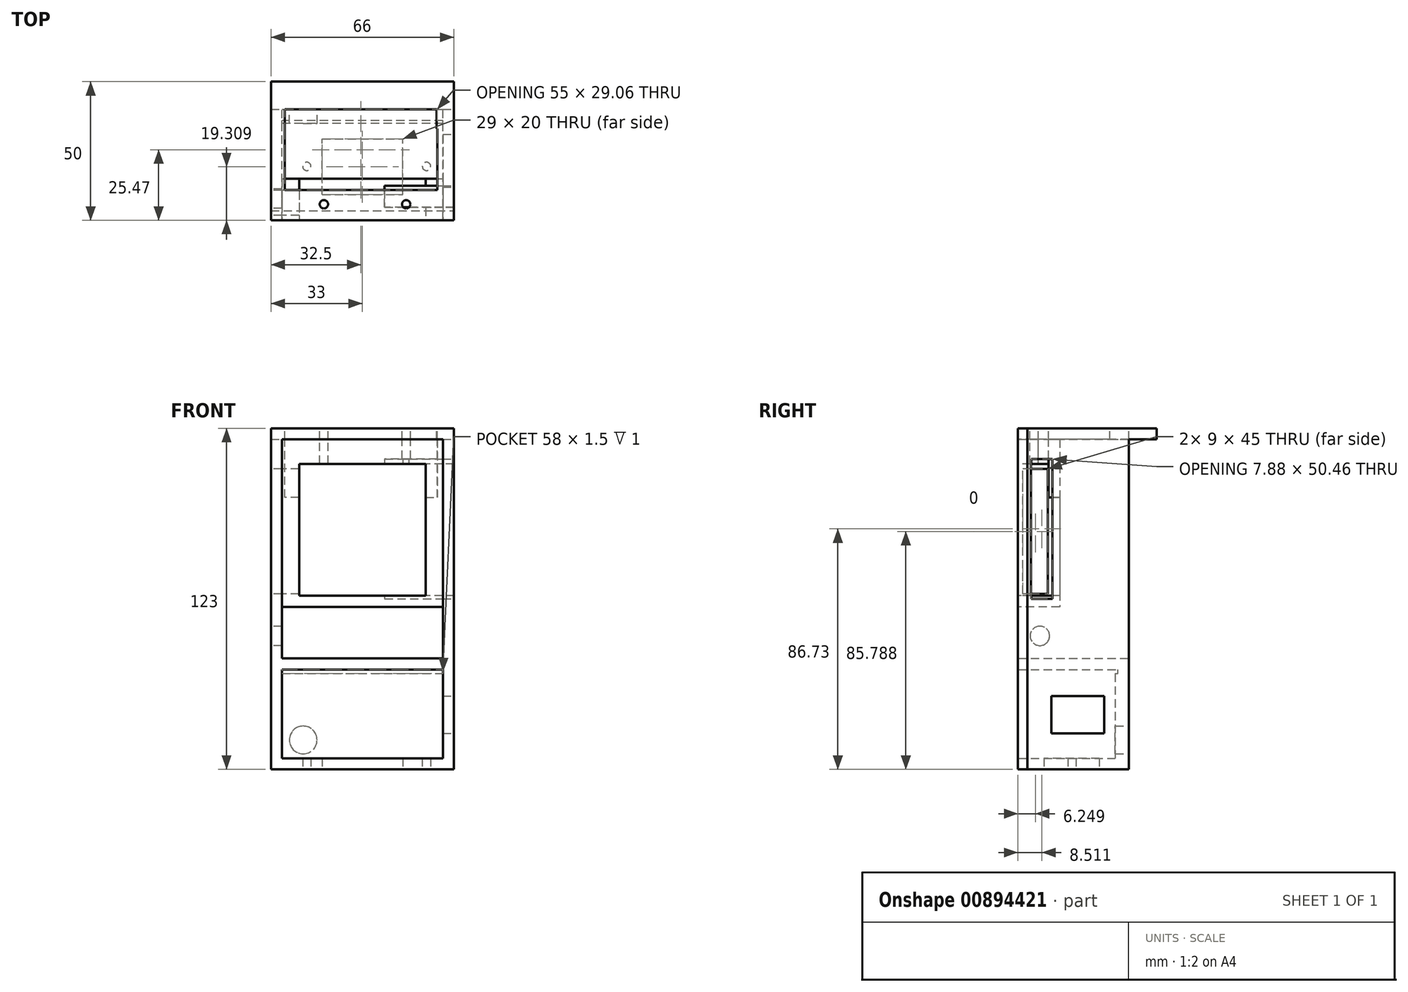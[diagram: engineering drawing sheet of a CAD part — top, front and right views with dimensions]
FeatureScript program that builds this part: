
annotation { "Feature Type Name" : "Feature", "Feature Type Description" : "" }
export const myFeature = defineFeature(function(context is Context, id is Id, definition is map)
    precondition{}
    {
        {
            var Q0;
            Q0=qCreatedBy(makeId("Front.planeOp"),FACE);
            var sketch = newSketch(context, id + "F0", { "sketchPlane" : qUnion([Q0])});
            skLineSegment(sketch, "E0.bottom", {"start": v(-29, 57.5) * mm, "end": v(29, 57.5) * mm});
            skLineSegment(sketch, "E0.top", {"start": v(-29, -57.5) * mm, "end": v(29, -57.5) * mm});
            skLineSegment(sketch, "E0.left", {"start": v(-29, 57.5) * mm, "end": v(-29, -57.5) * mm});
            skLineSegment(sketch, "E0.right", {"start": v(29, 57.5) * mm, "end": v(29, -57.5) * mm});
            skPoint(sketch, "E0.middle", {"position": v(0, 0) * mm});
            skLineSegment(sketch, "E1.0", {"start": v(-33, 61.5) * mm, "end": v(33, 61.5) * mm});
            skLineSegment(sketch, "E1.1", {"start": v(-33, 61.5) * mm, "end": v(-33, -61.5) * mm});
            skLineSegment(sketch, "E1.2", {"start": v(-33, -61.5) * mm, "end": v(33, -61.5) * mm});
            skLineSegment(sketch, "E1.3", {"start": v(33, 61.5) * mm, "end": v(33, -61.5) * mm});
            skLineSegment(sketch, "E2.bottom", {"start": v(-29, -21.5) * mm, "end": v(29, -21.5) * mm});
            skLineSegment(sketch, "E2.top", {"start": v(-29, -25.5) * mm, "end": v(29, -25.5) * mm});
            skLineSegment(sketch, "E2.left", {"start": v(-29, -21.5) * mm, "end": v(-29, -25.5) * mm});
            skLineSegment(sketch, "E2.right", {"start": v(29, -21.5) * mm, "end": v(29, -25.5) * mm});
            skPoint(sketch, "E3.end.orphan", {"position": v(-11.95, -21.5) * mm});
            skLineSegment(sketch, "E4", {"start": v(21.26, 35.1) * mm, "end": v(20.76, 35.1) * mm});
            skLineSegment(sketch, "E5.bottom", {"start": v(-21, 46.17) * mm, "end": v(21.26, 46.17) * mm});
            skLineSegment(sketch, "E5.top", {"start": v(-21, -2.9) * mm, "end": v(21.26, -2.9) * mm});
            skLineSegment(sketch, "E5.left", {"start": v(-21, 46.17) * mm, "end": v(-21, -2.9) * mm});
            skLineSegment(sketch, "E5.right", {"start": v(21.26, 46.17) * mm, "end": v(21.26, -2.9) * mm});
            skLineSegment(sketch, "E6", {"start": v(-29, -2.9) * mm, "end": v(-21, -2.9) * mm});
            skLineSegment(sketch, "E7", {"start": v(21.26, -2.9) * mm, "end": v(29, -2.9) * mm});
            skPoint(sketch, "E8.end.orphan", {"position": v(11.45, 46.17) * mm});
            skPoint(sketch, "E9.end.orphan", {"position": v(-21, 32.08) * mm});
            skLineSegment(sketch, "E10", {"start": v(0, 57.5) * mm, "end": v(0, -21.5) * mm});
            skSolve(sketch);
        }
        {
            var Q0;
            {var subQ6=sQuery(id+"F0.wireOp",EDGE,"E0.bottom");Q0=makeQuery(id+"F0.imprint","IMPRINT",FACE,{"disambiguationData":[TD([[makeQuery(id+"F0.imprint","IMPRINT",EDGE,{"derivedFrom":subQ6}),1.0]])]});}
            var Q1;
            Q1=makeQuery(id+"F0.imprint","IMPRINT",FACE,{"disambiguationData":[TD([[makeQuery(id+"F0.imprint","IMPRINT",EDGE,{"derivedFrom":sQuery(id+"F0.wireOp",EDGE,"E2.bottom")}),-1.0]])]});
            extrude(context, id + "F1", {"entities" : qUnion([Q0, Q1]), "depth" : 40 * mm, "offsetDistance" : 25 * mm});
        }
        {
            var Q0;
            Q0=makeQuery(id+"F1.opExtrude","CAP_FACE",FACE,{"disambiguationData":[OSD([sQuery(id+"F0.wireOp",EDGE,"E0.bottom"),sQuery(id+"F0.wireOp",EDGE,"E0.top"),sQuery(id+"F0.wireOp",EDGE,"E0.left"),sQuery(id+"F0.wireOp",EDGE,"E0.right"),sQuery(id+"F0.wireOp",EDGE,"E1.0"),sQuery(id+"F0.wireOp",EDGE,"E1.1"),sQuery(id+"F0.wireOp",EDGE,"E1.2"),sQuery(id+"F0.wireOp",EDGE,"E1.3"),sQuery(id+"F0.wireOp",EDGE,"E2.bottom"),sQuery(id+"F0.wireOp",EDGE,"E2.top")])],"isStart":false});
            var sketch = newSketch(context, id + "F2", { "sketchPlane" : qUnion([Q0])});
            skLineSegment(sketch, "E11", {"start": v(7.17, -21.5) * mm, "end": v(7.17, -1.5) * mm});
            skLineSegment(sketch, "E12.bottom", {"start": v(-22.77, 48.68) * mm, "end": v(22.77, 48.68) * mm});
            skLineSegment(sketch, "E12.top", {"start": v(-22.77, -2.9) * mm, "end": v(22.77, -2.9) * mm});
            skLineSegment(sketch, "E12.left", {"start": v(-22.77, 48.68) * mm, "end": v(-22.77, -2.9) * mm});
            skLineSegment(sketch, "E12.right", {"start": v(22.77, 48.68) * mm, "end": v(22.77, -2.9) * mm});
            skPoint(sketch, "E13.end.orphan", {"position": v(-17.23, 48.68) * mm});
            skPoint(sketch, "E14.end.orphan", {"position": v(-22.77, 26.8) * mm});
            skLineSegment(sketch, "E15.bottom", {"start": v(-29, -2.9) * mm, "end": v(29, -2.9) * mm});
            skLineSegment(sketch, "E15.top", {"start": v(-29, 1.1) * mm, "end": v(29, 1.1) * mm});
            skLineSegment(sketch, "E15.left", {"start": v(-29, -2.9) * mm, "end": v(-29, 1.1) * mm});
            skLineSegment(sketch, "E15.right", {"start": v(29, -2.9) * mm, "end": v(29, 1.1) * mm});
            skSolve(sketch);
        }
        {
            var Q0;
            {var subQ10=sQuery(id+"F2.wireOp",EDGE,"E12.bottom");Q0=makeQuery(id+"F2.imprint","IMPRINT",FACE,{"disambiguationData":[TD([[makeQuery(id+"F2.imprint","IMPRINT",EDGE,{"derivedFrom":subQ10}),1.0]])]});}
            var Q1;
            {var subQ0=sQuery(id+"F2.wireOp",EDGE,"E15.bottom");var subQ1=sQuery(id+"F2.wireOp",EDGE,"E12.left");var subQ2=makeQuery(id+"F2.imprint","INTERSECT",VERTEX,{"derivedFrom":[subQ1,subQ0]});Q1=makeQuery(id+"F2.imprint","IMPRINT",FACE,{"disambiguationData":[TD([[makeQuery(id+"F2.imprint","IMPRINT",EDGE,{"disambiguationData":[TD([[subQ2,1.0]])],"derivedFrom":subQ1}),1.0]])]});}
            var Q2;
            {var subQ5=sQuery(id+"F2.wireOp",EDGE,"E15.left");Q2=makeQuery(id+"F2.imprint","IMPRINT",FACE,{"disambiguationData":[TD([[makeQuery(id+"F2.imprint","IMPRINT",EDGE,{"derivedFrom":subQ5}),1.0]])]});}
            var Q3;
            {var subQ5=sQuery(id+"F2.wireOp",EDGE,"E15.right");Q3=makeQuery(id+"F2.imprint","IMPRINT",FACE,{"disambiguationData":[TD([[makeQuery(id+"F2.imprint","IMPRINT",EDGE,{"derivedFrom":subQ5}),-1.0]])]});}
            extrude(context, id + "F3", {"entities" : qUnion([Q0, Q1, Q2, Q3]), "oppositeDirection" : true, "depth" : 15 * mm, "offsetDistance" : 25 * mm});
        }
        {
            var Q0;
            Q0=makeQuery(id+"F1.opExtrude","SWEPT_FACE",FACE,{"disambiguationData":[OSD([sQuery(id+"F0.wireOp",EDGE,"E1.1")])]});
            var sketch = newSketch(context, id + "F4", { "sketchPlane" : qUnion([Q0])});
            skLineSegment(sketch, "E16.bottom", {"start": v(29.25, 1.79) * mm, "end": v(38.25, 1.79) * mm});
            skLineSegment(sketch, "E16.top", {"start": v(29.25, 46.79) * mm, "end": v(38.25, 46.79) * mm});
            skLineSegment(sketch, "E16.left", {"start": v(29.25, 1.79) * mm, "end": v(29.25, 46.79) * mm});
            skLineSegment(sketch, "E16.right", {"start": v(38.25, 1.79) * mm, "end": v(38.25, 46.79) * mm});
            skSolve(sketch);
        }
        {
            var Q0;
            Q0=makeQuery(id+"F4.imprint","IMPRINT",FACE,{"disambiguationData":[TD([[makeQuery(id+"F4.imprint","IMPRINT",EDGE,{"derivedFrom":sQuery(id+"F4.wireOp",EDGE,"E16.bottom")}),1.0]])]});
            extrude(context, id + "F5", {"entities" : qUnion([Q0]), "operationType" : NewBodyOperationType.REMOVE, "oppositeDirection" : true, "depth" : 25 * mm, "offsetDistance" : 25 * mm});
        }
        {
            var Q0;
            Q0=makeQuery(id+"F3.opExtrude","SWEPT_FACE",FACE,{"disambiguationData":[OSD([sQuery(id+"F0.wireOp",EDGE,"E0.left"),sQuery(id+"F2.wireOp",EDGE,"E15.left")])]});
            var sketch = newSketch(context, id + "F6", { "sketchPlane" : qUnion([Q0])});
            skLineSegment(sketch, "E17.bottom", {"start": v(29.37, 46.1) * mm, "end": v(38.95, 46.1) * mm});
            skLineSegment(sketch, "E17.top", {"start": v(29.37, 1.4) * mm, "end": v(38.95, 1.4) * mm});
            skLineSegment(sketch, "E17.left", {"start": v(29.37, 46.1) * mm, "end": v(29.37, 1.4) * mm});
            skLineSegment(sketch, "E17.right", {"start": v(38.95, 46.1) * mm, "end": v(38.95, 1.4) * mm});
            skSolve(sketch);
        }
        {
            var Q0;
            Q0=makeQuery(id+"F6.imprint","IMPRINT",FACE,{"disambiguationData":[TD([[makeQuery(id+"F6.imprint","IMPRINT",EDGE,{"derivedFrom":sQuery(id+"F6.wireOp",EDGE,"E17.bottom")}),-1.0]])]});
            extrude(context, id + "F7", {"entities" : qUnion([Q0]), "operationType" : NewBodyOperationType.REMOVE, "oppositeDirection" : true, "depth" : 25 * mm, "offsetDistance" : 25 * mm});
        }
        {
            var Q0;
            Q0=makeQuery(id+"F1.opExtrude","SWEPT_FACE",FACE,{"disambiguationData":[OSD([sQuery(id+"F0.wireOp",EDGE,"E1.2")])]});
            var sketch = newSketch(context, id + "F8", { "sketchPlane" : qUnion([Q0])});
            skLineSegment(sketch, "E18", {"start": v(0, 0) * mm, "end": v(0, 10.7) * mm});
            skLineSegment(sketch, "E19", {"start": v(0, 19.37) * mm, "end": v(-25, 19.37) * mm});
            skLineSegment(sketch, "E20", {"start": v(0, 19.37) * mm, "end": v(25, 19.37) * mm});
            skLineSegment(sketch, "E21.bottom", {"start": v(-14.5, 30.7) * mm, "end": v(14.5, 30.7) * mm});
            skLineSegment(sketch, "E21.top", {"start": v(-14.5, 10.7) * mm, "end": v(14.5, 10.7) * mm});
            skLineSegment(sketch, "E21.left", {"start": v(-14.5, 30.7) * mm, "end": v(-14.5, 10.7) * mm});
            skLineSegment(sketch, "E21.right", {"start": v(14.5, 30.7) * mm, "end": v(14.5, 10.7) * mm});
            skPoint(sketch, "E22", {"position": v(25, 19.37) * mm});
            skPoint(sketch, "E23", {"position": v(-25, 19.37) * mm});
            skPoint(sketch, "E24.end.orphan", {"position": v(-14.5, 15.72) * mm});
            skPoint(sketch, "E25.end.orphan", {"position": v(0, 30.7) * mm});
            skSolve(sketch);
        }
        {
            var Q0;
            {var subQ0=sQuery(id+"F8.wireOp",EDGE,"E21.top");var subQ1=makeQuery(id+"F8.imprint","IMPRINT",VERTEX,{"derivedFrom":subQ0});Q0=makeQuery(id+"F8.imprint","IMPRINT",FACE,{"disambiguationData":[TD([[makeQuery(id+"F8.imprint","IMPRINT",EDGE,{"disambiguationData":[TD([[subQ1,1.0]])],"derivedFrom":subQ0}),1.0]])]});}
            var Q1;
            {var subQ0=sQuery(id+"F8.wireOp",EDGE,"E21.bottom");Q1=makeQuery(id+"F8.imprint","IMPRINT",FACE,{"disambiguationData":[TD([[makeQuery(id+"F8.imprint","IMPRINT",EDGE,{"derivedFrom":subQ0}),-1.0]])]});}
            extrude(context, id + "F9", {"entities" : qUnion([Q0, Q1]), "operationType" : NewBodyOperationType.REMOVE, "oppositeDirection" : true, "depth" : 25 * mm, "offsetDistance" : 25 * mm});
        }
        {
            var Q0;
            Q0=makeQuery(id+"F1.opExtrude","SWEPT_FACE",FACE,{"disambiguationData":[OSD([sQuery(id+"F0.wireOp",EDGE,"E1.3")])]});
            var sketch = newSketch(context, id + "F10", { "sketchPlane" : qUnion([Q0])});
            skLineSegment(sketch, "E26.bottom", {"start": v(-9, -35.07) * mm, "end": v(-28, -35.07) * mm});
            skLineSegment(sketch, "E26.top", {"start": v(-9, -48.57) * mm, "end": v(-28, -48.57) * mm});
            skLineSegment(sketch, "E26.left", {"start": v(-9, -35.07) * mm, "end": v(-9, -48.57) * mm});
            skLineSegment(sketch, "E26.right", {"start": v(-28, -35.07) * mm, "end": v(-28, -48.57) * mm});
            skSolve(sketch);
        }
        {
            var Q0;
            Q0=makeQuery(id+"F10.imprint","IMPRINT",FACE,{"disambiguationData":[TD([[makeQuery(id+"F10.imprint","IMPRINT",EDGE,{"derivedFrom":sQuery(id+"F10.wireOp",EDGE,"E26.bottom")}),1.0]])]});
            extrude(context, id + "F11", {"entities" : qUnion([Q0]), "operationType" : NewBodyOperationType.REMOVE, "oppositeDirection" : true, "depth" : 25 * mm, "offsetDistance" : 25 * mm});
        }
        {
            var Q0;
            Q0=makeQuery(id+"F1.opExtrude","SWEPT_FACE",FACE,{"disambiguationData":[OSD([sQuery(id+"F0.wireOp",EDGE,"E1.2")])]});
            var sketch = newSketch(context, id + "F12", { "sketchPlane" : qUnion([Q0])});
            skPoint(sketch, "E27", {"position": v(-20.04, 20.56) * mm});
            skPoint(sketch, "E28", {"position": v(23.1, 20.56) * mm});
            skPoint(sketch, "E29.start.orphan", {"position": v(0, 30.7) * mm});
            skSolve(sketch);
        }
        {
            var Q0;
            Q0=makeQuery(id+"F1.opExtrude","SWEPT_FACE",FACE,{"disambiguationData":[OSD([sQuery(id+"F0.wireOp",EDGE,"E1.2")])]});
            var sketch = newSketch(context, id + "F13", { "sketchPlane" : qUnion([Q0])});
            skLineSegment(sketch, "E30.bottom", {"start": v(-33, 40) * mm, "end": v(33, 40) * mm});
            skLineSegment(sketch, "E30.top", {"start": v(-33, 36.62) * mm, "end": v(33, 36.62) * mm});
            skLineSegment(sketch, "E30.left", {"start": v(-33, 40) * mm, "end": v(-33, 36.62) * mm});
            skLineSegment(sketch, "E30.right", {"start": v(33, 40) * mm, "end": v(33, 36.62) * mm});
            skSolve(sketch);
        }
        {
            var Q0;
            Q0=sQuery(id+"F12.wireOp",VERTEX,"E28");
            var Q1;
            Q1=sQuery(id+"F12.wireOp",VERTEX,"E27");
            var Q2;
            Q2=makeQuery(id+"F1.opExtrude","SWEPT_BODY",BODY,{"disambiguationData":[OSD([sQuery(id+"F0.wireOp",EDGE,"E0.bottom"),sQuery(id+"F0.wireOp",EDGE,"E0.top"),sQuery(id+"F0.wireOp",EDGE,"E0.left"),sQuery(id+"F0.wireOp",EDGE,"E0.right"),sQuery(id+"F0.wireOp",EDGE,"E1.0"),sQuery(id+"F0.wireOp",EDGE,"E1.1"),sQuery(id+"F0.wireOp",EDGE,"E1.2"),sQuery(id+"F0.wireOp",EDGE,"E1.3"),sQuery(id+"F0.wireOp",EDGE,"E2.bottom"),sQuery(id+"F0.wireOp",EDGE,"E2.top")])]});
            hole(context, id + "F14", {"style" : HoleStyle.SIMPLE, "endStyle" : HoleEndStyle.BLIND, "holeDiameter" : 3 * mm, "majorDiameter" : 5 * mm, "holeDepth" : 6 * mm, "isTappedThrough" : true, "tappedDepth" : 12 * mm, "tapClearance" : 3, "startFromSketch" : true, "locations" : qUnion([Q0, Q1]), "scope" : qUnion([Q2])});
        }
        {
            var Q0;
            {var subQ3=sQuery(id+"F13.wireOp",EDGE,"E30.top");Q0=makeQuery(id+"F13.imprint","IMPRINT",FACE,{"disambiguationData":[TD([[makeQuery(id+"F13.imprint","IMPRINT",EDGE,{"derivedFrom":subQ3}),-1.0]])]});}
            var sketch = newSketch(context, id + "F15", { "sketchPlane" : qUnion([Q0])});
            skLineSegment(sketch, "E31.bottom", {"start": v(32.9, 0) * mm, "end": v(-32.92, 0) * mm});
            skLineSegment(sketch, "E31.top", {"start": v(32.9, 5) * mm, "end": v(-32.92, 5) * mm});
            skLineSegment(sketch, "E31.left", {"start": v(32.9, 0) * mm, "end": v(32.9, 5) * mm});
            skLineSegment(sketch, "E31.right", {"start": v(-32.92, 0) * mm, "end": v(-32.92, 5) * mm});
            skSolve(sketch);
        }
        {
            var Q0;
            Q0=makeQuery(id+"F15.imprint","IMPRINT",FACE,{"disambiguationData":[TD([[makeQuery(id+"F15.imprint","IMPRINT",EDGE,{"derivedFrom":sQuery(id+"F15.wireOp",EDGE,"E31.bottom")}),1.0]])]});
            extrude(context, id + "F16", {"entities" : qUnion([Q0]), "operationType" : NewBodyOperationType.ADD, "oppositeDirection" : true, "depth" : 34.5 * mm, "offsetDistance" : 25 * mm});
        }
        {
            var Q0;
            Q0=makeQuery(id+"F1.opExtrude","SWEPT_FACE",FACE,{"disambiguationData":[OSD([sQuery(id+"F0.wireOp",EDGE,"E1.0")])]});
            var sketch = newSketch(context, id + "F17", { "sketchPlane" : qUnion([Q0])});
            skLineSegment(sketch, "E32.bottom", {"start": v(27, -6.92) * mm, "end": v(-28, -6.92) * mm});
            skLineSegment(sketch, "E32.top", {"start": v(27, -29.06) * mm, "end": v(-28, -29.06) * mm});
            skLineSegment(sketch, "E32.left", {"start": v(27, -6.92) * mm, "end": v(27, -29.06) * mm});
            skLineSegment(sketch, "E32.right", {"start": v(-28, -6.92) * mm, "end": v(-28, -29.06) * mm});
            skLineSegment(sketch, "E33", {"start": v(-28, -20) * mm, "end": v(-33, -20) * mm});
            skPoint(sketch, "E33.startSnap0", {"position": v(-33, -20) * mm});
            skLineSegment(sketch, "E34", {"start": v(33, -14.47) * mm, "end": v(27, -14.47) * mm});
            skSolve(sketch);
        }
        {
            var Q0;
            {var subQ3=sQuery(id+"F17.wireOp",EDGE,"E32.bottom");Q0=makeQuery(id+"F17.imprint","IMPRINT",FACE,{"disambiguationData":[TD([[makeQuery(id+"F17.imprint","IMPRINT",EDGE,{"derivedFrom":subQ3}),1.0]])]});}
            extrude(context, id + "F18", {"entities" : qUnion([Q0]), "operationType" : NewBodyOperationType.REMOVE, "oppositeDirection" : true, "depth" : 25 * mm, "offsetDistance" : 25 * mm});
        }
        {
            var Q0;
            Q0=makeQuery(id+"F1.opExtrude","SWEPT_FACE",FACE,{"disambiguationData":[OSD([sQuery(id+"F0.wireOp",EDGE,"E1.0")])]});
            var sketch = newSketch(context, id + "F19", { "sketchPlane" : qUnion([Q0])});
            skPoint(sketch, "E35", {"position": v(15.8, -34.24) * mm});
            skPoint(sketch, "E36", {"position": v(-13.9, -34.24) * mm});
            skSolve(sketch);
        }
        {
            var Q0;
            Q0=sQuery(id+"F19.wireOp",VERTEX,"E35");
            var Q1;
            Q1=sQuery(id+"F19.wireOp",VERTEX,"E36");
            var Q2;
            Q2=makeQuery(id+"F1.opExtrude","SWEPT_BODY",BODY,{"disambiguationData":[OSD([sQuery(id+"F0.wireOp",EDGE,"E0.bottom"),sQuery(id+"F0.wireOp",EDGE,"E0.top"),sQuery(id+"F0.wireOp",EDGE,"E0.left"),sQuery(id+"F0.wireOp",EDGE,"E0.right"),sQuery(id+"F0.wireOp",EDGE,"E1.0"),sQuery(id+"F0.wireOp",EDGE,"E1.1"),sQuery(id+"F0.wireOp",EDGE,"E1.2"),sQuery(id+"F0.wireOp",EDGE,"E1.3"),sQuery(id+"F0.wireOp",EDGE,"E2.bottom"),sQuery(id+"F0.wireOp",EDGE,"E2.top")])]});
            var Q3;
            Q3=makeQuery(id+"F3.opExtrude","SWEPT_BODY",BODY,{"disambiguationData":[OSD([sQuery(id+"F0.wireOp",EDGE,"E0.bottom"),sQuery(id+"F0.wireOp",EDGE,"E0.left"),sQuery(id+"F0.wireOp",EDGE,"E0.right"),sQuery(id+"F2.wireOp",EDGE,"E12.bottom"),sQuery(id+"F2.wireOp",EDGE,"E12.left"),sQuery(id+"F2.wireOp",EDGE,"E12.right"),sQuery(id+"F2.wireOp",EDGE,"E15.bottom"),sQuery(id+"F2.wireOp",EDGE,"E15.top"),sQuery(id+"F2.wireOp",EDGE,"E15.left"),sQuery(id+"F2.wireOp",EDGE,"E15.right")])]});
            hole(context, id + "F20", {"style" : HoleStyle.SIMPLE, "endStyle" : HoleEndStyle.BLIND, "holeDiameter" : 3 * mm, "majorDiameter" : 5 * mm, "holeDepth" : 15 * mm, "isTappedThrough" : true, "tappedDepth" : 12 * mm, "tapClearance" : 3, "startFromSketch" : true, "locations" : qUnion([Q0, Q1]), "scope" : qUnion([Q2, Q3])});
        }
        {
            var Q0;
            Q0=makeQuery(id+"F1.opExtrude","SWEPT_FACE",FACE,{"disambiguationData":[OSD([sQuery(id+"F0.wireOp",EDGE,"E1.1")])]});
            var sketch = newSketch(context, id + "F21", { "sketchPlane" : qUnion([Q0])});
            skPoint(sketch, "E37", {"position": v(32.13, -13.37) * mm});
            skSolve(sketch);
        }
        {
            var Q0;
            Q0=sQuery(id+"F21.wireOp",VERTEX,"E37");
            var Q1;
            Q1=makeQuery(id+"F1.opExtrude","SWEPT_BODY",BODY,{"disambiguationData":[OSD([sQuery(id+"F0.wireOp",EDGE,"E0.bottom"),sQuery(id+"F0.wireOp",EDGE,"E0.top"),sQuery(id+"F0.wireOp",EDGE,"E0.left"),sQuery(id+"F0.wireOp",EDGE,"E0.right"),sQuery(id+"F0.wireOp",EDGE,"E1.0"),sQuery(id+"F0.wireOp",EDGE,"E1.1"),sQuery(id+"F0.wireOp",EDGE,"E1.2"),sQuery(id+"F0.wireOp",EDGE,"E1.3"),sQuery(id+"F0.wireOp",EDGE,"E2.bottom"),sQuery(id+"F0.wireOp",EDGE,"E2.top")])]});
            hole(context, id + "F22", {"style" : HoleStyle.SIMPLE, "endStyle" : HoleEndStyle.BLIND, "holeDiameter" : 7 * mm, "majorDiameter" : 5 * mm, "holeDepth" : 15 * mm, "isTappedThrough" : true, "tappedDepth" : 12 * mm, "tapClearance" : 3, "startFromSketch" : true, "locations" : qUnion([Q0]), "scope" : qUnion([Q1])});
        }
        {
            var Q0;
            {var subQ3=sQuery(id+"F13.wireOp",EDGE,"E30.top");Q0=makeQuery(id+"F13.imprint","IMPRINT",FACE,{"disambiguationData":[TD([[makeQuery(id+"F13.imprint","IMPRINT",EDGE,{"derivedFrom":subQ3}),-1.0]])]});}
            var sketch = newSketch(context, id + "F23", { "sketchPlane" : qUnion([Q0])});
            skLineSegment(sketch, "E38.bottom", {"start": v(-33.05, 0) * mm, "end": v(32.95, 0) * mm});
            skLineSegment(sketch, "E38.top", {"start": v(-33.05, 4) * mm, "end": v(32.95, 4) * mm});
            skLineSegment(sketch, "E38.left", {"start": v(-33.05, 0) * mm, "end": v(-33.05, 4) * mm});
            skLineSegment(sketch, "E38.right", {"start": v(32.95, 0) * mm, "end": v(32.95, 4) * mm});
            skSolve(sketch);
        }
        {
            var Q0;
            {var subQ6=sQuery(id+"F23.wireOp",EDGE,"E38.right");Q0=makeQuery(id+"F23.imprint","IMPRINT",FACE,{"disambiguationData":[TD([[makeQuery(id+"F23.imprint","IMPRINT",EDGE,{"derivedFrom":subQ6}),1.0]])]});}
            extrude(context, id + "F24", {"entities" : qUnion([Q0]), "operationType" : NewBodyOperationType.ADD, "oppositeDirection" : true, "depth" : 37.7 * mm, "offsetDistance" : 25 * mm});
        }
        {
            var Q0;
            Q0=makeQuery(id+"F24.boolean.opBoolean","MERGE",FACE,{"derivedFrom":[makeQuery(id+"F16.boolean.opBoolean","MERGE",FACE,{"derivedFrom":[makeQuery(id+"F1.opExtrude","CAP_FACE",FACE,{"disambiguationData":[OSD([sQuery(id+"F0.wireOp",EDGE,"E0.bottom"),sQuery(id+"F0.wireOp",EDGE,"E0.top"),sQuery(id+"F0.wireOp",EDGE,"E0.left"),sQuery(id+"F0.wireOp",EDGE,"E0.right"),sQuery(id+"F0.wireOp",EDGE,"E1.0"),sQuery(id+"F0.wireOp",EDGE,"E1.1"),sQuery(id+"F0.wireOp",EDGE,"E1.2"),sQuery(id+"F0.wireOp",EDGE,"E1.3"),sQuery(id+"F0.wireOp",EDGE,"E2.bottom"),sQuery(id+"F0.wireOp",EDGE,"E2.top")])],"isStart":true}),makeQuery(id+"F16.opExtrude","SWEPT_FACE",FACE,{"disambiguationData":[OSD([sQuery(id+"F15.wireOp",EDGE,"E31.bottom")])]})]}),makeQuery(id+"F24.opExtrude","SWEPT_FACE",FACE,{"disambiguationData":[OSD([sQuery(id+"F23.wireOp",EDGE,"E38.bottom")])]})]});
            var sketch = newSketch(context, id + "F25", { "sketchPlane" : qUnion([Q0])});
            skPoint(sketch, "E39", {"position": v(21.36, -50.9) * mm});
            skSolve(sketch);
        }
        {
            var Q0;
            Q0=sQuery(id+"F25.wireOp",VERTEX,"E39");
            var Q1;
            Q1=makeQuery(id+"F1.opExtrude","SWEPT_BODY",BODY,{"disambiguationData":[OSD([sQuery(id+"F0.wireOp",EDGE,"E0.bottom"),sQuery(id+"F0.wireOp",EDGE,"E0.top"),sQuery(id+"F0.wireOp",EDGE,"E0.left"),sQuery(id+"F0.wireOp",EDGE,"E0.right"),sQuery(id+"F0.wireOp",EDGE,"E1.0"),sQuery(id+"F0.wireOp",EDGE,"E1.1"),sQuery(id+"F0.wireOp",EDGE,"E1.2"),sQuery(id+"F0.wireOp",EDGE,"E1.3"),sQuery(id+"F0.wireOp",EDGE,"E2.bottom"),sQuery(id+"F0.wireOp",EDGE,"E2.top")])]});
            hole(context, id + "F26", {"style" : HoleStyle.SIMPLE, "endStyle" : HoleEndStyle.BLIND, "holeDiameter" : 10 * mm, "majorDiameter" : 5 * mm, "holeDepth" : 15 * mm, "isTappedThrough" : true, "tappedDepth" : 12 * mm, "tapClearance" : 3, "startFromSketch" : true, "locations" : qUnion([Q0]), "scope" : qUnion([Q1])});
        }
        {
            var Q0;
            Q0=makeQuery(id+"F24.boolean.opBoolean","MERGE",FACE,{"derivedFrom":[makeQuery(id+"F16.boolean.opBoolean","MERGE",FACE,{"derivedFrom":[makeQuery(id+"F1.opExtrude","CAP_FACE",FACE,{"disambiguationData":[OSD([sQuery(id+"F0.wireOp",EDGE,"E0.bottom"),sQuery(id+"F0.wireOp",EDGE,"E0.top"),sQuery(id+"F0.wireOp",EDGE,"E0.left"),sQuery(id+"F0.wireOp",EDGE,"E0.right"),sQuery(id+"F0.wireOp",EDGE,"E1.0"),sQuery(id+"F0.wireOp",EDGE,"E1.1"),sQuery(id+"F0.wireOp",EDGE,"E1.2"),sQuery(id+"F0.wireOp",EDGE,"E1.3"),sQuery(id+"F0.wireOp",EDGE,"E2.bottom"),sQuery(id+"F0.wireOp",EDGE,"E2.top")])],"isStart":true}),makeQuery(id+"F16.opExtrude","SWEPT_FACE",FACE,{"disambiguationData":[OSD([sQuery(id+"F15.wireOp",EDGE,"E31.bottom")])]})]}),makeQuery(id+"F24.opExtrude","SWEPT_FACE",FACE,{"disambiguationData":[OSD([sQuery(id+"F23.wireOp",EDGE,"E38.bottom")])]})]});
            var sketch = newSketch(context, id + "F27", { "sketchPlane" : qUnion([Q0])});
            skLineSegment(sketch, "E40.bottom", {"start": v(-33, 61.5) * mm, "end": v(33, 61.5) * mm});
            skLineSegment(sketch, "E40.top", {"start": v(-33, 57.5) * mm, "end": v(33, 57.5) * mm});
            skLineSegment(sketch, "E40.left", {"start": v(-33, 61.5) * mm, "end": v(-33, 57.5) * mm});
            skLineSegment(sketch, "E40.right", {"start": v(33, 61.5) * mm, "end": v(33, 57.5) * mm});
            skSolve(sketch);
        }
        {
            var Q0;
            Q0=makeQuery(id+"F27.imprint","IMPRINT",FACE,{"disambiguationData":[TD([[makeQuery(id+"F27.imprint","IMPRINT",EDGE,{"derivedFrom":sQuery(id+"F27.wireOp",EDGE,"E40.bottom")}),1.0]])]});
            extrude(context, id + "F28", {"entities" : qUnion([Q0]), "operationType" : NewBodyOperationType.ADD, "depth" : 10 * mm, "offsetDistance" : 25 * mm});
        }
        {
            var Q0;
            Q0=makeQuery(id+"F28.boolean.opBoolean","MERGE",FACE,{"derivedFrom":[makeQuery(id+"F1.opExtrude","SWEPT_FACE",FACE,{"disambiguationData":[OSD([sQuery(id+"F0.wireOp",EDGE,"E1.0")])]}),makeQuery(id+"F28.opExtrude","SWEPT_FACE",FACE,{"disambiguationData":[OSD([sQuery(id+"F27.wireOp",EDGE,"E40.bottom")])]})]});
            var sketch = newSketch(context, id + "F29", { "sketchPlane" : qUnion([Q0])});
            skLineSegment(sketch, "E41.bottom", {"start": v(-28, -6.92) * mm, "end": v(26.8, -6.92) * mm});
            skLineSegment(sketch, "E41.top", {"start": v(-28, 0) * mm, "end": v(26.8, 0) * mm});
            skLineSegment(sketch, "E41.left", {"start": v(-28, -6.92) * mm, "end": v(-28, 0) * mm});
            skLineSegment(sketch, "E41.right", {"start": v(26.8, -6.92) * mm, "end": v(26.8, 0) * mm});
            skSolve(sketch);
        }
        {
            var Q0;
            Q0=makeQuery(id+"F29.imprint","IMPRINT",FACE,{"disambiguationData":[TD([[makeQuery(id+"F29.imprint","IMPRINT",EDGE,{"derivedFrom":sQuery(id+"F29.wireOp",EDGE,"E41.bottom")}),-1.0]])]});
            extrude(context, id + "F30", {"entities" : qUnion([Q0]), "operationType" : NewBodyOperationType.REMOVE, "oppositeDirection" : true, "depth" : 25 * mm, "offsetDistance" : 25 * mm});
        }
        {
            var Q0;
            Q0=makeQuery(id+"F13.imprint","IMPRINT",FACE,{"disambiguationData":[TD([[makeQuery(id+"F13.imprint","IMPRINT",EDGE,{"derivedFrom":sQuery(id+"F13.wireOp",EDGE,"E30.bottom")}),-1.0]])]});
            extrude(context, id + "F31", {"entities" : qUnion([Q0]), "oppositeDirection" : true, "depth" : 122.9 * mm, "offsetDistance" : 25 * mm});
        }
        {
            var Q0;
            Q0=makeQuery(id+"F28.boolean.opBoolean","MERGE",FACE,{"derivedFrom":[makeQuery(id+"F1.opExtrude","SWEPT_FACE",FACE,{"disambiguationData":[OSD([sQuery(id+"F0.wireOp",EDGE,"E1.3")])]}),makeQuery(id+"F28.opExtrude","SWEPT_FACE",FACE,{"disambiguationData":[OSD([sQuery(id+"F27.wireOp",EDGE,"E40.left")])]})]});
            var sketch = newSketch(context, id + "F32", { "sketchPlane" : qUnion([Q0])});
            skLineSegment(sketch, "E42.bottom", {"start": v(-35.28, 50.46) * mm, "end": v(-27.55, 50.46) * mm});
            skLineSegment(sketch, "E42.top", {"start": v(-35.28, 0) * mm, "end": v(-27.55, 0) * mm});
            skLineSegment(sketch, "E42.left", {"start": v(-35.28, 50.46) * mm, "end": v(-35.28, 0) * mm});
            skLineSegment(sketch, "E42.right", {"start": v(-27.55, 50.46) * mm, "end": v(-27.55, 0) * mm});
            skSolve(sketch);
        }
        {
            var Q0;
            Q0=makeQuery(id+"F32.imprint","IMPRINT",FACE,{"disambiguationData":[TD([[makeQuery(id+"F32.imprint","IMPRINT",EDGE,{"derivedFrom":sQuery(id+"F32.wireOp",EDGE,"E42.bottom")}),-1.0]])]});
            extrude(context, id + "F33", {"entities" : qUnion([Q0]), "operationType" : NewBodyOperationType.REMOVE, "oppositeDirection" : true, "depth" : 25 * mm, "offsetDistance" : 25 * mm});
        }
        {
            var Q0;
            Q0=makeQuery(id+"F3.opExtrude","SWEPT_FACE",FACE,{"disambiguationData":[OSD([sQuery(id+"F2.wireOp",EDGE,"E12.right")])]});
            var sketch = newSketch(context, id + "F34", { "sketchPlane" : qUnion([Q0])});
            skLineSegment(sketch, "E43.bottom", {"start": v(27.13, 1.1) * mm, "end": v(35.43, 1.1) * mm});
            skLineSegment(sketch, "E43.top", {"start": v(27.13, 50.92) * mm, "end": v(35.43, 50.92) * mm});
            skLineSegment(sketch, "E43.left", {"start": v(27.13, 1.1) * mm, "end": v(27.13, 50.92) * mm});
            skLineSegment(sketch, "E43.right", {"start": v(35.43, 1.1) * mm, "end": v(35.43, 50.92) * mm});
            skSolve(sketch);
        }
        {
            var Q0;
            Q0=makeQuery(id+"F34.imprint","IMPRINT",FACE,{"disambiguationData":[TD([[makeQuery(id+"F34.imprint","IMPRINT",EDGE,{"derivedFrom":sQuery(id+"F34.wireOp",EDGE,"E43.bottom")}),1.0]])]});
            extrude(context, id + "F35", {"entities" : qUnion([Q0]), "operationType" : NewBodyOperationType.REMOVE, "oppositeDirection" : true, "depth" : 25 * mm, "offsetDistance" : 25 * mm});
        }
    });
